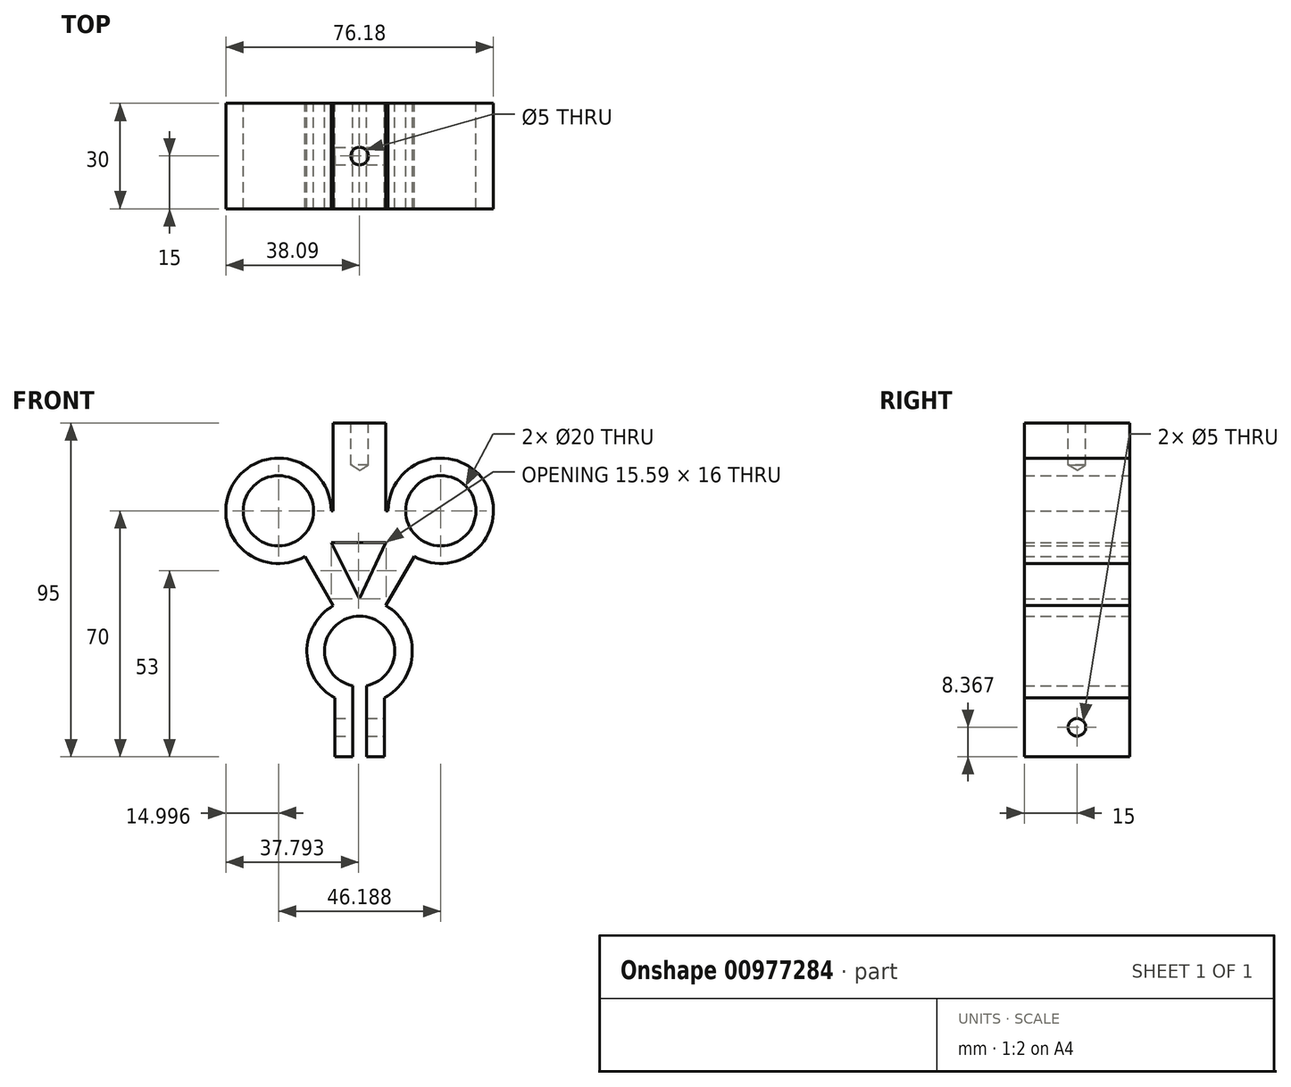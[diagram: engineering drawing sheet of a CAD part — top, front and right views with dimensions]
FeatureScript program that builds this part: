
annotation { "Feature Type Name" : "Feature", "Feature Type Description" : "" }
export const myFeature = defineFeature(function(context is Context, id is Id, definition is map)
    precondition{}
    {
        {
            var Q0;
            Q0=qCreatedBy(makeId("Front.planeOp"),FACE);
            var sketch = newSketch(context, id + "F0", { "sketchPlane" : qUnion([Q0])});
            skCircle(sketch, "E0", {"center": v(0, 0) * mm, "radius": 10 * mm});
            skCircle(sketch, "E1", {"center": v(23.1, 40) * mm, "radius": 10 * mm});
            skCircle(sketch, "E2", {"center": v(-23.1, 40) * mm, "radius": 10 * mm});
            skCircle(sketch, "E3", {"center": v(-23.1, 40) * mm, "radius": 15 * mm});
            skCircle(sketch, "E4", {"center": v(23.1, 40) * mm, "radius": 15 * mm});
            skCircle(sketch, "E5", {"center": v(0, 0) * mm, "radius": 15 * mm});
            skLineSegment(sketch, "E6", {"start": v(0, 0) * mm, "end": v(-23.1, 40) * mm});
            skLineSegment(sketch, "E7", {"start": v(23.1, 40) * mm, "end": v(0, 0) * mm});
            skLineSegment(sketch, "E8", {"start": v(-23.1, 40) * mm, "end": v(23.1, 40) * mm});
            skLineSegment(sketch, "E9.bottom", {"start": v(-2, 0) * mm, "end": v(2, 0) * mm});
            skLineSegment(sketch, "E9.top", {"start": v(-2, -30) * mm, "end": v(2, -30) * mm});
            skLineSegment(sketch, "E9.left", {"start": v(-2, 0) * mm, "end": v(-2, -30) * mm});
            skLineSegment(sketch, "E9.right", {"start": v(2, 0) * mm, "end": v(2, -30) * mm});
            skPoint(sketch, "E9.middle", {"position": v(0, -15) * mm});
            skLineSegment(sketch, "E10.bottom", {"start": v(7, -30) * mm, "end": v(-7, -30) * mm});
            skLineSegment(sketch, "E10.top", {"start": v(7, 0) * mm, "end": v(-7, 0) * mm});
            skLineSegment(sketch, "E10.left", {"start": v(7, -30) * mm, "end": v(7, 0) * mm});
            skLineSegment(sketch, "E10.right", {"start": v(-7, -30) * mm, "end": v(-7, 0) * mm});
            skLineSegment(sketch, "E11.bottom", {"start": v(-7.5, 65) * mm, "end": v(7.5, 65) * mm});
            skLineSegment(sketch, "E11.top", {"start": v(-7.5, 15) * mm, "end": v(7.5, 15) * mm});
            skLineSegment(sketch, "E11.left", {"start": v(-7.5, 65) * mm, "end": v(-7.5, 15) * mm});
            skLineSegment(sketch, "E11.right", {"start": v(7.5, 65) * mm, "end": v(7.5, 15) * mm});
            skPoint(sketch, "E11.middle", {"position": v(0, 40) * mm});
            skSolve(sketch);
        }
        {
            var Q0;
            {var subQ0=sQuery(id+"F0.wireOp",EDGE,"E7");var subQ1=sQuery(id+"F0.wireOp",EDGE,"E1");var subQ2=makeQuery(id+"F0.imprint","INTERSECT",VERTEX,{"derivedFrom":[subQ1,subQ0]});Q0=makeQuery(id+"F0.imprint","IMPRINT",FACE,{"disambiguationData":[TD([[makeQuery(id+"F0.imprint","IMPRINT",EDGE,{"disambiguationData":[TD([[subQ2,-1.0]])],"derivedFrom":subQ1}),-1.0]])]});}
            var Q1;
            {var subQ0=sQuery(id+"F0.wireOp",EDGE,"E6");var subQ1=sQuery(id+"F0.wireOp",EDGE,"E2");var subQ2=makeQuery(id+"F0.imprint","INTERSECT",VERTEX,{"derivedFrom":[subQ1,subQ0]});Q1=makeQuery(id+"F0.imprint","IMPRINT",FACE,{"disambiguationData":[TD([[makeQuery(id+"F0.imprint","IMPRINT",EDGE,{"disambiguationData":[TD([[subQ2,1.0]])],"derivedFrom":subQ1}),-1.0]])]});}
            var Q2;
            {var subQ0=sQuery(id+"F0.wireOp",EDGE,"E10.right");var subQ1=sQuery(id+"F0.wireOp",EDGE,"E5");var subQ2=makeQuery(id+"F0.imprint","INTERSECT",VERTEX,{"derivedFrom":[subQ1,subQ0]});Q2=makeQuery(id+"F0.imprint","IMPRINT",FACE,{"disambiguationData":[TD([[makeQuery(id+"F0.imprint","IMPRINT",EDGE,{"disambiguationData":[TD([[subQ2,-1.0]])],"derivedFrom":subQ1}),-1.0]])]});}
            var Q3;
            {var subQ0=sQuery(id+"F0.wireOp",EDGE,"E10.left");var subQ1=sQuery(id+"F0.wireOp",EDGE,"E5");var subQ2=makeQuery(id+"F0.imprint","INTERSECT",VERTEX,{"derivedFrom":[subQ1,subQ0]});Q3=makeQuery(id+"F0.imprint","IMPRINT",FACE,{"disambiguationData":[TD([[makeQuery(id+"F0.imprint","IMPRINT",EDGE,{"disambiguationData":[TD([[subQ2,1.0]])],"derivedFrom":subQ1}),-1.0]])]});}
            var Q4;
            {var subQ0=sQuery(id+"F0.wireOp",EDGE,"E6");var subQ1=sQuery(id+"F0.wireOp",EDGE,"E0");var subQ2=makeQuery(id+"F0.imprint","INTERSECT",VERTEX,{"derivedFrom":[subQ1,subQ0]});Q4=makeQuery(id+"F0.imprint","IMPRINT",FACE,{"disambiguationData":[TD([[makeQuery(id+"F0.imprint","IMPRINT",EDGE,{"disambiguationData":[TD([[subQ2,-1.0]])],"derivedFrom":subQ1}),-1.0]])]});}
            var Q5;
            {var subQ0=sQuery(id+"F0.wireOp",EDGE,"E7");var subQ1=sQuery(id+"F0.wireOp",EDGE,"E0");var subQ2=makeQuery(id+"F0.imprint","INTERSECT",VERTEX,{"derivedFrom":[subQ1,subQ0]});Q5=makeQuery(id+"F0.imprint","IMPRINT",FACE,{"disambiguationData":[TD([[makeQuery(id+"F0.imprint","IMPRINT",EDGE,{"disambiguationData":[TD([[subQ2,1.0]])],"derivedFrom":subQ1}),-1.0]])]});}
            var Q6;
            {var subQ0=sQuery(id+"F0.wireOp",EDGE,"E7");var subQ1=sQuery(id+"F0.wireOp",EDGE,"E1");var subQ2=makeQuery(id+"F0.imprint","INTERSECT",VERTEX,{"derivedFrom":[subQ1,subQ0]});Q6=makeQuery(id+"F0.imprint","IMPRINT",FACE,{"disambiguationData":[TD([[makeQuery(id+"F0.imprint","IMPRINT",EDGE,{"disambiguationData":[TD([[subQ2,1.0]])],"derivedFrom":subQ1}),-1.0]])]});}
            var Q7;
            {var subQ0=sQuery(id+"F0.wireOp",EDGE,"E6");var subQ1=sQuery(id+"F0.wireOp",EDGE,"E2");var subQ2=makeQuery(id+"F0.imprint","INTERSECT",VERTEX,{"derivedFrom":[subQ1,subQ0]});Q7=makeQuery(id+"F0.imprint","IMPRINT",FACE,{"disambiguationData":[TD([[makeQuery(id+"F0.imprint","IMPRINT",EDGE,{"disambiguationData":[TD([[subQ2,-1.0]])],"derivedFrom":subQ1}),-1.0]])]});}
            var Q8;
            {var subQ0=sQuery(id+"F0.wireOp",EDGE,"E6");var subQ5=sQuery(id+"F0.wireOp",EDGE,"E3");var subQ6=makeQuery(id+"F0.imprint","INTERSECT",VERTEX,{"derivedFrom":[subQ5,subQ0]});Q8=makeQuery(id+"F0.imprint","IMPRINT",FACE,{"disambiguationData":[TD([[makeQuery(id+"F0.imprint","IMPRINT",EDGE,{"disambiguationData":[TD([[subQ6,-1.0]])],"derivedFrom":subQ5}),-1.0]])]});}
            var Q9;
            {var subQ0=sQuery(id+"F0.wireOp",EDGE,"E6");var subQ1=sQuery(id+"F0.wireOp",EDGE,"E0");var subQ2=makeQuery(id+"F0.imprint","INTERSECT",VERTEX,{"derivedFrom":[subQ1,subQ0]});Q9=makeQuery(id+"F0.imprint","IMPRINT",FACE,{"disambiguationData":[TD([[makeQuery(id+"F0.imprint","IMPRINT",EDGE,{"disambiguationData":[TD([[subQ2,1.0]])],"derivedFrom":subQ1}),-1.0]])]});}
            var Q10;
            {var subQ0=sQuery(id+"F0.wireOp",EDGE,"E10.right");var subQ1=sQuery(id+"F0.wireOp",EDGE,"E0");var subQ2=makeQuery(id+"F0.imprint","INTERSECT",VERTEX,{"derivedFrom":[subQ1,subQ0]});Q10=makeQuery(id+"F0.imprint","IMPRINT",FACE,{"disambiguationData":[TD([[makeQuery(id+"F0.imprint","IMPRINT",EDGE,{"disambiguationData":[TD([[subQ2,-1.0]])],"derivedFrom":subQ1}),-1.0]])]});}
            var Q11;
            {var subQ0=sQuery(id+"F0.wireOp",EDGE,"E9.right");var subQ1=sQuery(id+"F0.wireOp",EDGE,"E0");var subQ2=makeQuery(id+"F0.imprint","INTERSECT",VERTEX,{"derivedFrom":[subQ1,subQ0]});Q11=makeQuery(id+"F0.imprint","IMPRINT",FACE,{"disambiguationData":[TD([[makeQuery(id+"F0.imprint","IMPRINT",EDGE,{"disambiguationData":[TD([[subQ2,-1.0]])],"derivedFrom":subQ1}),-1.0]])]});}
            var Q12;
            {var subQ5=sQuery(id+"F0.wireOp",EDGE,"E11.top");Q12=makeQuery(id+"F0.imprint","IMPRINT",FACE,{"disambiguationData":[TD([[makeQuery(id+"F0.imprint","IMPRINT",EDGE,{"derivedFrom":subQ5}),1.0]])]});}
            var Q13;
            {var subQ5=sQuery(id+"F0.wireOp",EDGE,"E11.bottom");Q13=makeQuery(id+"F0.imprint","IMPRINT",FACE,{"disambiguationData":[TD([[makeQuery(id+"F0.imprint","IMPRINT",EDGE,{"derivedFrom":subQ5}),-1.0]])]});}
            var Q14;
            {var subQ1=sQuery(id+"F0.wireOp",EDGE,"E4");var subQ5=sQuery(id+"F0.wireOp",EDGE,"E7");var subQ6=makeQuery(id+"F0.imprint","INTERSECT",VERTEX,{"derivedFrom":[subQ1,subQ5]});Q14=makeQuery(id+"F0.imprint","IMPRINT",FACE,{"disambiguationData":[TD([[makeQuery(id+"F0.imprint","IMPRINT",EDGE,{"disambiguationData":[TD([[subQ6,1.0]])],"derivedFrom":subQ1}),-1.0]])]});}
            extrude(context, id + "F1", {"entities" : qUnion([Q0, Q1, Q2, Q3, Q4, Q5, Q6, Q7, Q8, Q9, Q10, Q11, Q12, Q13, Q14]), "depth" : 30 * mm, "offsetDistance" : 25 * mm});
        }
        {
            var Q0;
            Q0=makeQuery(id+"F1.opExtrude","SWEPT_FACE",FACE,{"disambiguationData":[OSD([sQuery(id+"F0.wireOp",EDGE,"E11.bottom")])]});
            var sketch = newSketch(context, id + "F2", { "sketchPlane" : qUnion([Q0])});
            skPoint(sketch, "E12", {"position": v(0, -15) * mm});
            skPoint(sketch, "E12.positionSnap0", {"position": v(-7.5, -15) * mm});
            skSolve(sketch);
        }
        {
            var Q0;
            Q0=sQuery(id+"F2.wireOp",VERTEX,"E12");
            var Q1;
            Q1=makeQuery(id+"F1.opExtrude","SWEPT_BODY",BODY,{"disambiguationData":[OSD([sQuery(id+"F0.wireOp",EDGE,"E0"),sQuery(id+"F0.wireOp",EDGE,"E1"),sQuery(id+"F0.wireOp",EDGE,"E2"),sQuery(id+"F0.wireOp",EDGE,"E3"),sQuery(id+"F0.wireOp",EDGE,"E4"),sQuery(id+"F0.wireOp",EDGE,"E5"),sQuery(id+"F0.wireOp",EDGE,"E6"),sQuery(id+"F0.wireOp",EDGE,"E7"),sQuery(id+"F0.wireOp",EDGE,"E8"),sQuery(id+"F0.wireOp",EDGE,"E9.left"),sQuery(id+"F0.wireOp",EDGE,"E9.right"),sQuery(id+"F0.wireOp",EDGE,"E10.bottom"),sQuery(id+"F0.wireOp",EDGE,"E10.left"),sQuery(id+"F0.wireOp",EDGE,"E10.right"),sQuery(id+"F0.wireOp",EDGE,"E11.bottom"),sQuery(id+"F0.wireOp",EDGE,"E11.left"),sQuery(id+"F0.wireOp",EDGE,"E11.right")])]});
            hole(context, id + "F3", {"style" : HoleStyle.SIMPLE, "endStyle" : HoleEndStyle.BLIND, "holeDiameter" : 5 * mm, "majorDiameter" : 5 * mm, "holeDepth" : 12 * mm, "isTappedThrough" : true, "tappedDepth" : 12 * mm, "tapClearance" : 3, "locations" : qUnion([Q0]), "scope" : qUnion([Q1])});
        }
        {
            var Q0;
            Q0=makeQuery(id+"F1.opExtrude","SWEPT_FACE",FACE,{"disambiguationData":[OSD([sQuery(id+"F0.wireOp",EDGE,"E10.left")])]});
            var sketch = newSketch(context, id + "F4", { "sketchPlane" : qUnion([Q0])});
            skPoint(sketch, "E13", {"position": v(-15, -21.63) * mm});
            skPoint(sketch, "E13.positionSnap0", {"position": v(0, -21.63) * mm});
            skPoint(sketch, "E13.positionSnap1", {"position": v(-15, -30) * mm});
            skCircle(sketch, "E14", {"center": v(-15, -21.63) * mm, "radius": 2.5 * mm});
            skSolve(sketch);
        }
        {
            var Q0;
            Q0=makeQuery(id+"F4.imprint","IMPRINT",FACE,{"disambiguationData":[TD([[makeQuery(id+"F4.imprint","IMPRINT",EDGE,{"derivedFrom":sQuery(id+"F4.wireOp",EDGE,"E14")}),1.0]])]});
            extrude(context, id + "F5", {"entities" : qUnion([Q0]), "operationType" : NewBodyOperationType.REMOVE, "oppositeDirection" : true, "depth" : 25 * mm, "offsetDistance" : 25 * mm});
        }
        {
            var Q0;
            Q0=makeQuery(id+"F1.opExtrude","CAP_FACE",FACE,{"disambiguationData":[OSD([sQuery(id+"F0.wireOp",EDGE,"E0"),sQuery(id+"F0.wireOp",EDGE,"E1"),sQuery(id+"F0.wireOp",EDGE,"E2"),sQuery(id+"F0.wireOp",EDGE,"E3"),sQuery(id+"F0.wireOp",EDGE,"E4"),sQuery(id+"F0.wireOp",EDGE,"E5"),sQuery(id+"F0.wireOp",EDGE,"E6"),sQuery(id+"F0.wireOp",EDGE,"E7"),sQuery(id+"F0.wireOp",EDGE,"E8"),sQuery(id+"F0.wireOp",EDGE,"E9.left"),sQuery(id+"F0.wireOp",EDGE,"E9.right"),sQuery(id+"F0.wireOp",EDGE,"E10.bottom"),sQuery(id+"F0.wireOp",EDGE,"E10.left"),sQuery(id+"F0.wireOp",EDGE,"E10.right"),sQuery(id+"F0.wireOp",EDGE,"E11.bottom"),sQuery(id+"F0.wireOp",EDGE,"E11.left"),sQuery(id+"F0.wireOp",EDGE,"E11.right")])],"isStart":true});
            var sketch = newSketch(context, id + "F6", { "sketchPlane" : qUnion([Q0])});
            skLineSegment(sketch, "E15", {"start": v(0, 15) * mm, "end": v(8.1, 31) * mm});
            skLineSegment(sketch, "E16", {"start": v(8.1, 31) * mm, "end": v(-7.5, 31) * mm});
            skLineSegment(sketch, "E17", {"start": v(-7.5, 31) * mm, "end": v(0, 15) * mm});
            skSolve(sketch);
        }
        {
            var Q0;
            Q0=qSketchRegion(id+"F6",true);
            extrude(context, id + "F7", {"entities" : qUnion([Q0]), "operationType" : NewBodyOperationType.REMOVE, "oppositeDirection" : true, "depth" : 40 * mm, "offsetDistance" : 25 * mm});
        }
    });
